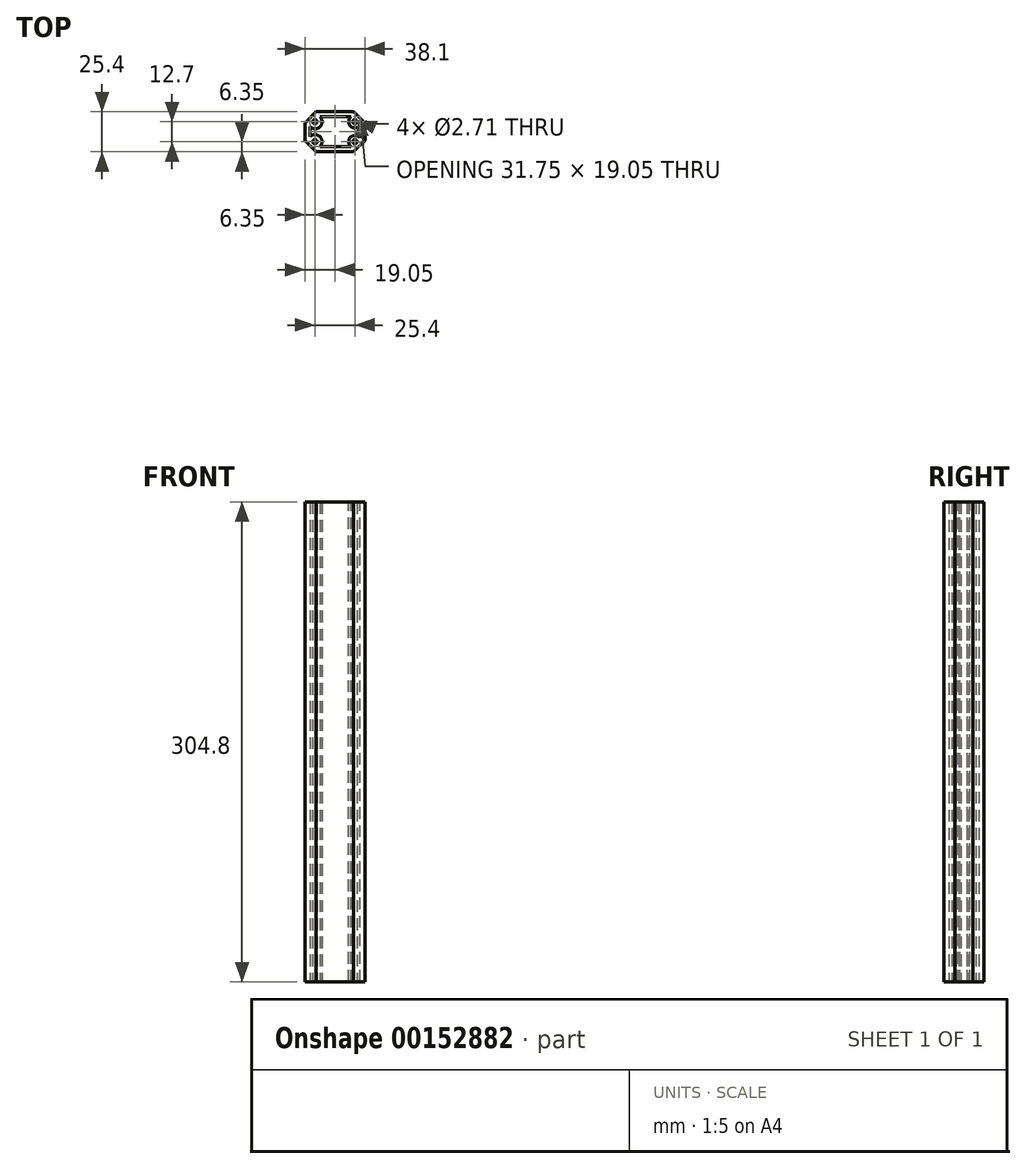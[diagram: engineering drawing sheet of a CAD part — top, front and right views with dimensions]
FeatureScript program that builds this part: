
annotation { "Feature Type Name" : "Feature", "Feature Type Description" : "" }
export const myFeature = defineFeature(function(context is Context, id is Id, definition is map)
    precondition{}
    {
        {
            var Q0;
            Q0=qCreatedBy(makeId("Top.planeOp"),FACE);
            var sketch = newSketch(context, id + "F0", { "sketchPlane" : qUnion([Q0])});
            skLineSegment(sketch, "E0", {"start": v(-11.96, 0) * mm, "end": v(-19.05, -7.09) * mm});
            skLineSegment(sketch, "E1", {"start": v(-11.96, 0) * mm, "end": v(11.96, 0) * mm});
            skCircle(sketch, "E2", {"center": v(12.7, -19.05) * mm, "radius": 1.35 * mm});
            skLineSegment(sketch, "E3", {"start": v(-11.96, -25.4) * mm, "end": v(11.96, -25.4) * mm});
            skLineSegment(sketch, "E4", {"start": v(-19.05, -7.09) * mm, "end": v(-19.05, -18.31) * mm});
            skLineSegment(sketch, "E5", {"start": v(-19.05, -18.31) * mm, "end": v(-11.96, -25.4) * mm});
            skLineSegment(sketch, "E6", {"start": v(11.96, 0) * mm, "end": v(19.05, -7.09) * mm});
            skLineSegment(sketch, "E7", {"start": v(19.05, -7.09) * mm, "end": v(19.05, -18.31) * mm});
            skLineSegment(sketch, "E8", {"start": v(19.05, -18.31) * mm, "end": v(11.96, -25.4) * mm});
            skCircle(sketch, "E9", {"center": v(-12.7, -19.05) * mm, "radius": 1.35 * mm});
            skCircle(sketch, "E10", {"center": v(12.7, -6.35) * mm, "radius": 1.35 * mm});
            skCircle(sketch, "E11", {"center": v(-12.7, -6.35) * mm, "radius": 1.35 * mm});
            skLineSegment(sketch, "E12", {"start": v(15.5, -3.54) * mm, "end": v(12.7, -6.35) * mm, "construction": true});
            skLineSegment(sketch, "E13", {"start": v(0, 0) * mm, "end": v(0, -25.4) * mm, "construction": true});
            skLineSegment(sketch, "E14.bottom", {"start": v(12.7, -6.35) * mm, "end": v(-12.7, -6.35) * mm, "construction": true});
            skLineSegment(sketch, "E14.top", {"start": v(12.7, -19.05) * mm, "end": v(-12.7, -19.05) * mm, "construction": true});
            skLineSegment(sketch, "E14.left", {"start": v(12.7, -6.35) * mm, "end": v(12.7, -19.05) * mm, "construction": true});
            skLineSegment(sketch, "E14.right", {"start": v(-12.7, -6.35) * mm, "end": v(-12.7, -19.05) * mm, "construction": true});
            skPoint(sketch, "E14.middle", {"position": v(0, -12.7) * mm});
            skLineSegment(sketch, "E15", {"start": v(12.7, -12.7) * mm, "end": v(19.05, -12.7) * mm, "construction": true});
            skLineSegment(sketch, "E16", {"start": v(-12.7, -12.7) * mm, "end": v(-19.05, -12.7) * mm, "construction": true});
            skSolve(sketch);
        }
        {
            var Q0;
            Q0=qSketchRegion(id+"F0",true);
            extrude(context, id + "F1", {"entities" : qUnion([Q0]), "depth" : 304.8 * mm});
        }
        {
            var Q0;
            Q0=makeQuery(id+"F1.opExtrude","CAP_FACE",FACE,{"disambiguationData":[OSD([sQuery(id+"F0.wireOp",EDGE,"XEPYvsBn-YUR1-ND3i-Hliu-0bTDEalwyczA.top"),sQuery(id+"F0.wireOp",EDGE,"XEPYvsBn-YUR1-ND3i-Hliu-0bTDEalwyczA.left"),sQuery(id+"F0.wireOp",EDGE,"XEPYvsBn-YUR1-ND3i-Hliu-0bTDEalwyczA.right"),sQuery(id+"F0.wireOp",EDGE,"xVlwOPhJ-aCTn-OcWs-i2q0-JGyUUewlvZk0"),sQuery(id+"F0.wireOp",EDGE,"E0"),sQuery(id+"F0.wireOp",EDGE,"E1"),sQuery(id+"F0.wireOp",EDGE,"E2"),sQuery(id+"F0.wireOp",EDGE,"E3"),sQuery(id+"F0.wireOp",EDGE,"E4"),sQuery(id+"F0.wireOp",EDGE,"E5"),sQuery(id+"F0.wireOp",EDGE,"E6"),sQuery(id+"F0.wireOp",EDGE,"E7"),sQuery(id+"F0.wireOp",EDGE,"E8"),sQuery(id+"F0.wireOp",EDGE,"E9"),sQuery(id+"F0.wireOp",EDGE,"E10"),sQuery(id+"F0.wireOp",EDGE,"E11")])],"isStart":false});
            shell(context, id + "F2", {"entities" : qUnion([Q0]), "thickness" : 3.17 * mm});
        }
        {
            var Q0;
            Q0=makeQuery(id+"F2.opShell","OFFSET_FACE",FACE,{"disambiguationData":[OSD([sQuery(id+"F0.wireOp",EDGE,"E0"),sQuery(id+"F0.wireOp",EDGE,"E1"),sQuery(id+"F0.wireOp",EDGE,"E2"),sQuery(id+"F0.wireOp",EDGE,"E3"),sQuery(id+"F0.wireOp",EDGE,"E4"),sQuery(id+"F0.wireOp",EDGE,"E5"),sQuery(id+"F0.wireOp",EDGE,"E6"),sQuery(id+"F0.wireOp",EDGE,"E7"),sQuery(id+"F0.wireOp",EDGE,"E8"),sQuery(id+"F0.wireOp",EDGE,"E9"),sQuery(id+"F0.wireOp",EDGE,"E10"),sQuery(id+"F0.wireOp",EDGE,"E11")])]});
            var Q1;
            Q1=makeQuery(id+"F1.opExtrude","CAP_FACE",FACE,{"disambiguationData":[OSD([sQuery(id+"F0.wireOp",EDGE,"E0"),sQuery(id+"F0.wireOp",EDGE,"E1"),sQuery(id+"F0.wireOp",EDGE,"E2"),sQuery(id+"F0.wireOp",EDGE,"E3"),sQuery(id+"F0.wireOp",EDGE,"E4"),sQuery(id+"F0.wireOp",EDGE,"E5"),sQuery(id+"F0.wireOp",EDGE,"E6"),sQuery(id+"F0.wireOp",EDGE,"E7"),sQuery(id+"F0.wireOp",EDGE,"E8"),sQuery(id+"F0.wireOp",EDGE,"E9"),sQuery(id+"F0.wireOp",EDGE,"E10"),sQuery(id+"F0.wireOp",EDGE,"E11")])],"isStart":true});
            extrude(context, id + "F3", {"entities" : qUnion([Q0]), "operationType" : NewBodyOperationType.REMOVE, "endBound" : BoundingType.UP_TO_SURFACE, "oppositeDirection" : true, "endBoundEntityFace" : qUnion([Q1]), "depth" : 25.4 * mm});
        }
        {
            var Q0;
            Q0=makeQuery(id+"F1.opExtrude","CAP_FACE",FACE,{"disambiguationData":[OSD([sQuery(id+"F0.wireOp",EDGE,"E0"),sQuery(id+"F0.wireOp",EDGE,"E1"),sQuery(id+"F0.wireOp",EDGE,"E2"),sQuery(id+"F0.wireOp",EDGE,"E3"),sQuery(id+"F0.wireOp",EDGE,"E4"),sQuery(id+"F0.wireOp",EDGE,"E5"),sQuery(id+"F0.wireOp",EDGE,"E6"),sQuery(id+"F0.wireOp",EDGE,"E7"),sQuery(id+"F0.wireOp",EDGE,"E8"),sQuery(id+"F0.wireOp",EDGE,"E9"),sQuery(id+"F0.wireOp",EDGE,"E10"),sQuery(id+"F0.wireOp",EDGE,"E11")])],"isStart":false});
            var sketch = newSketch(context, id + "F4", { "sketchPlane" : qUnion([Q0])});
            skLineSegment(sketch, "E17.bottom", {"start": v(9.9, -3.54) * mm, "end": v(10.26, -3.18) * mm});
            skLineSegment(sketch, "E17.top", {"start": v(15.5, -9.16) * mm, "end": v(15.88, -8.79) * mm});
            skLineSegment(sketch, "E17.left", {"start": v(9.9, -3.54) * mm, "end": v(15.5, -9.16) * mm, "construction": true});
            skLineSegment(sketch, "E17.right", {"start": v(10.26, -3.18) * mm, "end": v(15.88, -8.79) * mm, "construction": true});
            skLineSegment(sketch, "E18", {"start": v(13.07, -5.98) * mm, "end": v(15.5, -3.54) * mm, "construction": true});
            skArc(sketch, "E19", {"start": v(9.9, -3.54) * mm, "mid": v(9.9, -9.16) * mm, "end": v(15.5, -9.16) * mm});
            skLineSegment(sketch, "E20", {"start": v(10.26, -3.18) * mm, "end": v(9.47, -3.18) * mm});
            skLineSegment(sketch, "E21", {"start": v(15.88, -9.58) * mm, "end": v(15.88, -8.79) * mm});
            skLineSegment(sketch, "E22", {"start": v(15.88, -15.82) * mm, "end": v(15.88, -16.61) * mm});
            skLineSegment(sketch, "E23", {"start": v(9.47, -22.23) * mm, "end": v(10.26, -22.23) * mm});
            skLineSegment(sketch, "E24.bottom", {"start": v(10.26, -22.23) * mm, "end": v(15.88, -16.61) * mm, "construction": true});
            skLineSegment(sketch, "E24.top", {"start": v(9.9, -21.86) * mm, "end": v(15.5, -16.24) * mm, "construction": true});
            skLineSegment(sketch, "E24.left", {"start": v(10.26, -22.23) * mm, "end": v(9.9, -21.86) * mm});
            skLineSegment(sketch, "E24.right", {"start": v(15.88, -16.61) * mm, "end": v(15.5, -16.24) * mm});
            skArc(sketch, "E25", {"start": v(15.5, -16.24) * mm, "mid": v(9.9, -16.24) * mm, "end": v(9.9, -21.86) * mm});
            skArc(sketch, "E26", {"start": v(15.88, -15.82) * mm, "mid": v(9.5, -15.85) * mm, "end": v(9.47, -22.23) * mm});
            skArc(sketch, "E27", {"start": v(9.47, -3.18) * mm, "mid": v(9.5, -9.55) * mm, "end": v(15.88, -9.58) * mm});
            skSolve(sketch);
        }
        {
            var Q0;
            Q0 = qSketchRegion(id + "F4", true);
            var Q1;
            Q1=makeQuery(id+"F1.opExtrude","CAP_FACE",FACE,{"disambiguationData":[OSD([sQuery(id+"F0.wireOp",EDGE,"E0"),sQuery(id+"F0.wireOp",EDGE,"E1"),sQuery(id+"F0.wireOp",EDGE,"E2"),sQuery(id+"F0.wireOp",EDGE,"E3"),sQuery(id+"F0.wireOp",EDGE,"E4"),sQuery(id+"F0.wireOp",EDGE,"E5"),sQuery(id+"F0.wireOp",EDGE,"E6"),sQuery(id+"F0.wireOp",EDGE,"E7"),sQuery(id+"F0.wireOp",EDGE,"E8"),sQuery(id+"F0.wireOp",EDGE,"E9"),sQuery(id+"F0.wireOp",EDGE,"E10"),sQuery(id+"F0.wireOp",EDGE,"E11")])],"isStart":true});
            extrude(context, id + "F5", {"entities" : qUnion([Q0]), "operationType" : NewBodyOperationType.REMOVE, "endBound" : BoundingType.UP_TO_SURFACE, "oppositeDirection" : true, "endBoundEntityFace" : qUnion([Q1]), "depth" : 25.4 * mm});
        }
        {
            var Q0;
            Q0=makeQuery(id+"F1.opExtrude","CAP_FACE",FACE,{"disambiguationData":[OSD([sQuery(id+"F0.wireOp",EDGE,"E0"),sQuery(id+"F0.wireOp",EDGE,"E1"),sQuery(id+"F0.wireOp",EDGE,"E2"),sQuery(id+"F0.wireOp",EDGE,"E3"),sQuery(id+"F0.wireOp",EDGE,"E4"),sQuery(id+"F0.wireOp",EDGE,"E5"),sQuery(id+"F0.wireOp",EDGE,"E6"),sQuery(id+"F0.wireOp",EDGE,"E7"),sQuery(id+"F0.wireOp",EDGE,"E8"),sQuery(id+"F0.wireOp",EDGE,"E9"),sQuery(id+"F0.wireOp",EDGE,"E10"),sQuery(id+"F0.wireOp",EDGE,"E11")])],"isStart":false});
            var sketch = newSketch(context, id + "F6", { "sketchPlane" : qUnion([Q0])});
            skLineSegment(sketch, "E28", {"start": v(-15.87, -12.7) * mm, "end": v(15.88, -12.7) * mm, "construction": true});
            skCircle(sketch, "E29", {"center": v(0, -12.7) * mm, "radius": 1.35 * mm, "construction": true});
            skSolve(sketch);
        }
    });
